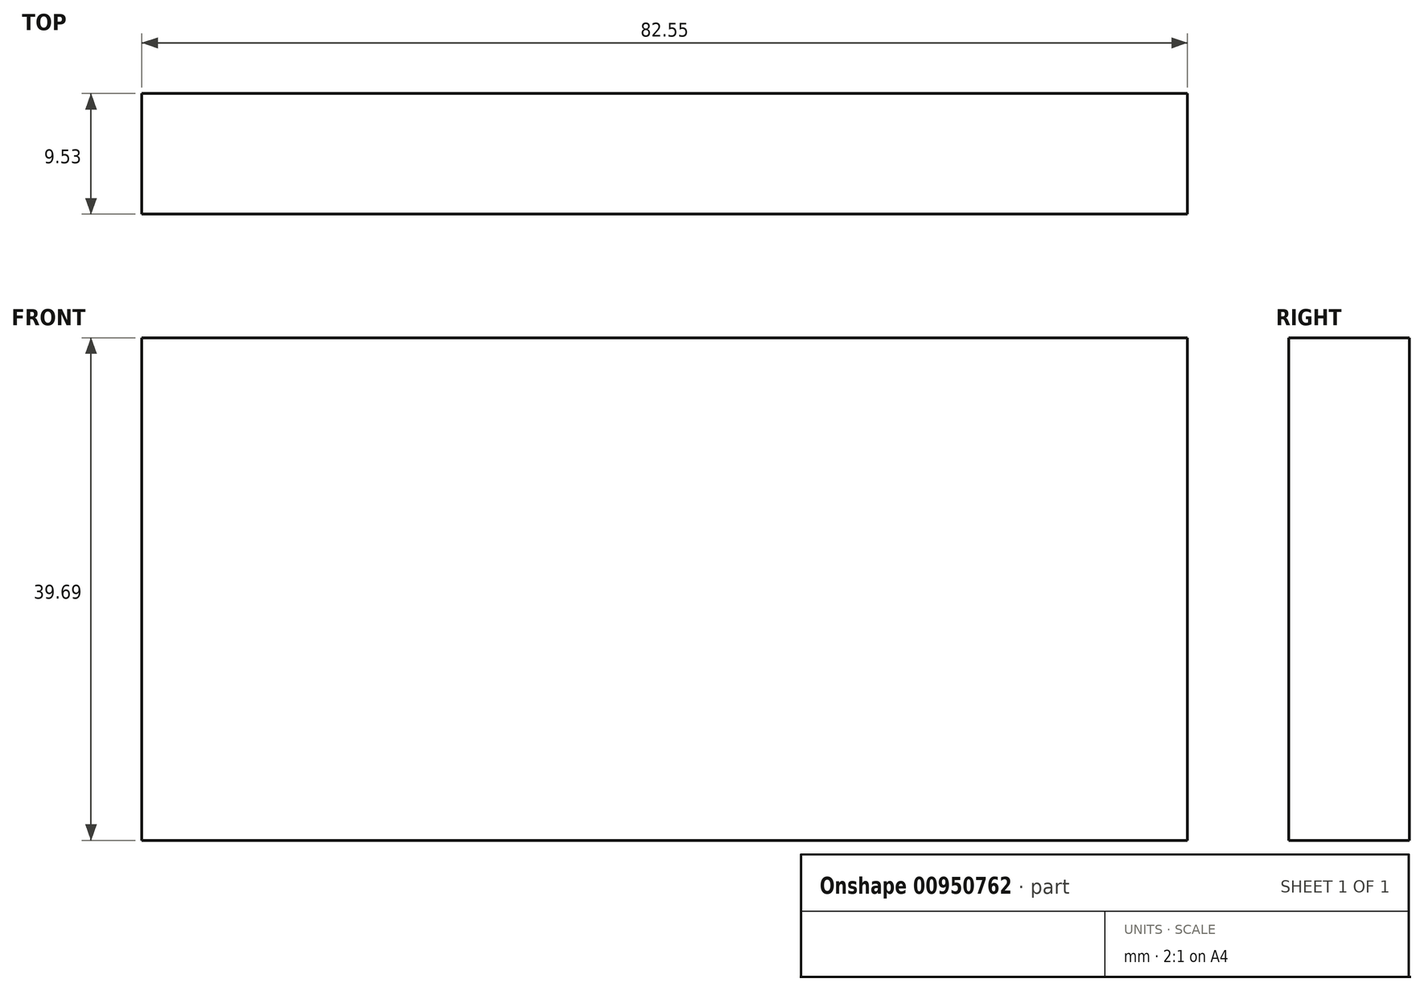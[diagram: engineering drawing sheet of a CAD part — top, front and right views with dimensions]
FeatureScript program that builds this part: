
annotation { "Feature Type Name" : "Feature", "Feature Type Description" : "" }
export const myFeature = defineFeature(function(context is Context, id is Id, definition is map)
    precondition{}
    {
        {
            var Q0;
            Q0=qCreatedBy(makeId("Front.planeOp"),FACE);
            var sketch = newSketch(context, id + "F0", { "sketchPlane" : qUnion([Q0])});
            skLineSegment(sketch, "E0.bottom", {"start": v(-32, 19.76) * mm, "end": v(50.56, 19.76) * mm});
            skLineSegment(sketch, "E0.top", {"start": v(-32, -19.93) * mm, "end": v(50.56, -19.93) * mm});
            skLineSegment(sketch, "E0.left", {"start": v(-32, 19.76) * mm, "end": v(-32, -19.93) * mm});
            skLineSegment(sketch, "E0.right", {"start": v(50.56, 19.76) * mm, "end": v(50.56, -19.93) * mm});
            skSolve(sketch);
        }
        {
            var Q0;
            Q0=makeQuery(id+"F0.imprint","IMPRINT",FACE,{"disambiguationData":[TD([[makeQuery(id+"F0.imprint","IMPRINT",EDGE,{"derivedFrom":sQuery(id+"F0.wireOp",EDGE,"E0.bottom")}),-1.0]])]});
            extrude(context, id + "F1", {"entities" : qUnion([Q0]), "depth" : 9.52 * mm, "offsetDistance" : 25.4 * mm});
        }
    });
